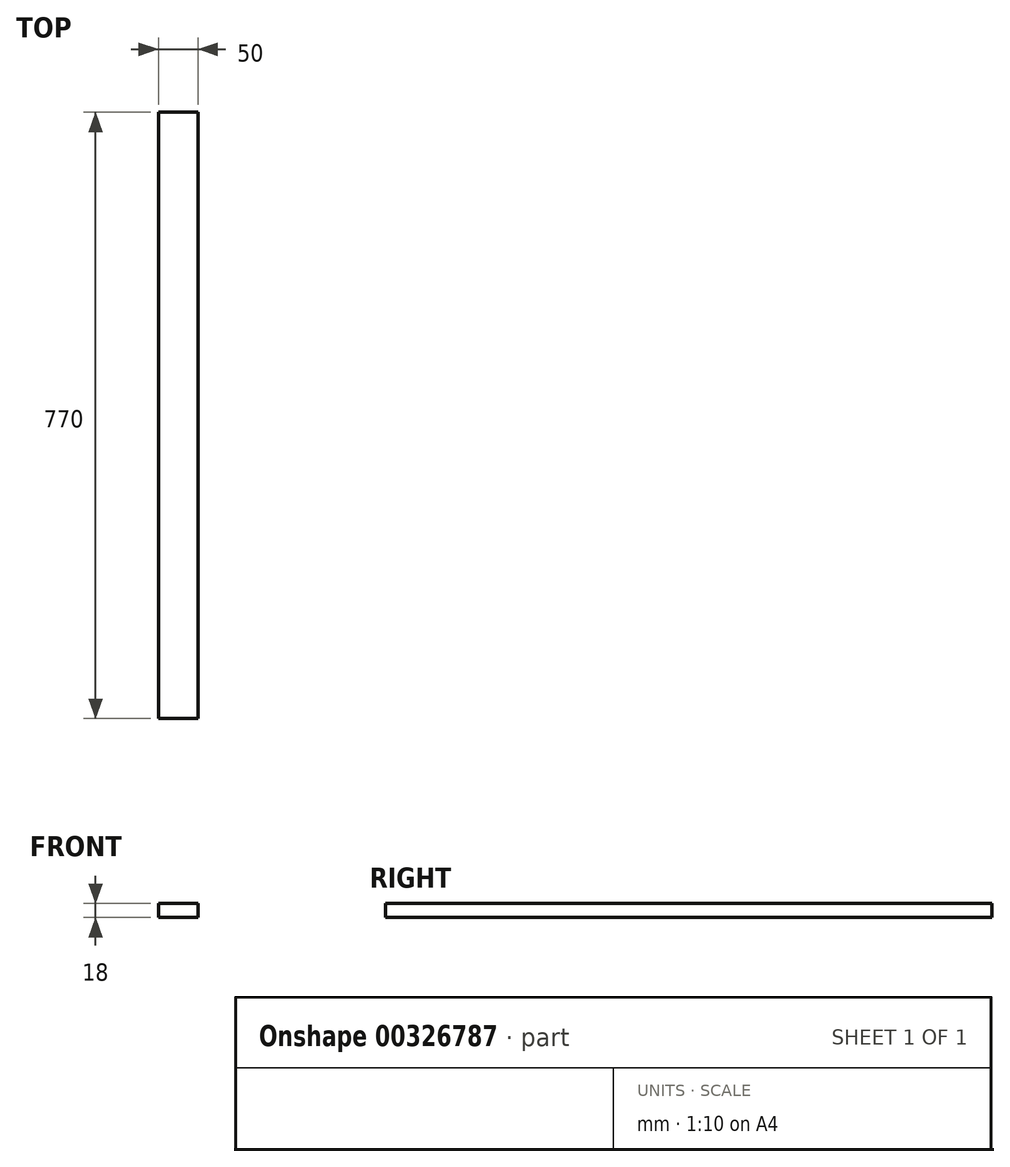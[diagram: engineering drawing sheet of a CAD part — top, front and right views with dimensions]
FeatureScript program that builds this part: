
annotation { "Feature Type Name" : "Feature", "Feature Type Description" : "" }
export const myFeature = defineFeature(function(context is Context, id is Id, definition is map)
    precondition{}
    {
        {
            var Q0;
            Q0=qCreatedBy(makeId("Top.planeOp"),FACE);
            var sketch = newSketch(context, id + "F0", { "sketchPlane" : qUnion([Q0])});
            skLineSegment(sketch, "E0.bottom", {"start": v(0, 0) * mm, "end": v(50, 0) * mm});
            skLineSegment(sketch, "E0.top", {"start": v(0, 770) * mm, "end": v(50, 770) * mm});
            skLineSegment(sketch, "E0.left", {"start": v(0, 0) * mm, "end": v(0, 770) * mm});
            skLineSegment(sketch, "E0.right", {"start": v(50, 0) * mm, "end": v(50, 770) * mm});
            skSolve(sketch);
        }
        {
            var Q0;
            Q0=qSketchRegion(id+"F0",true);
            extrude(context, id + "F1", {"entities" : qUnion([Q0]), "depth" : 18 * mm});
        }
    });
